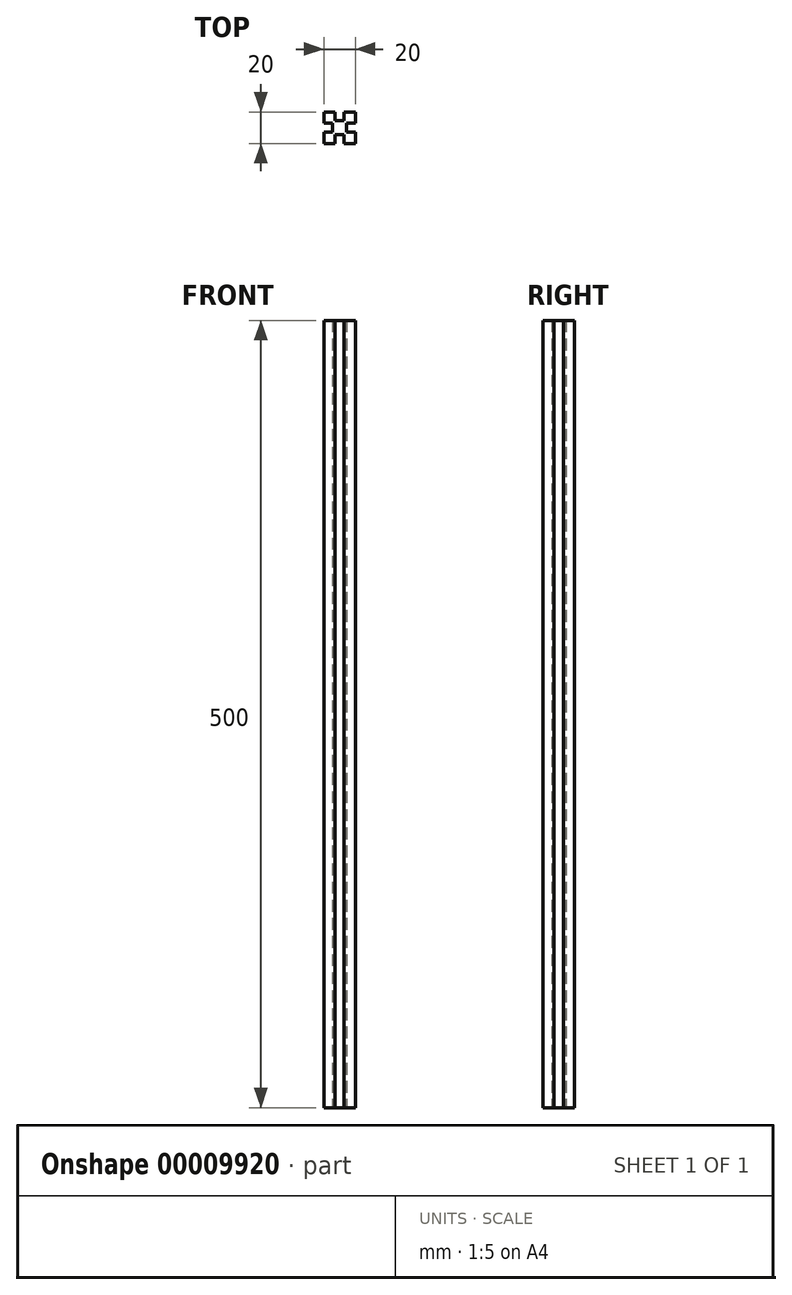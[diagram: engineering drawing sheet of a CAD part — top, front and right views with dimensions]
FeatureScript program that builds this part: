
annotation { "Feature Type Name" : "Feature", "Feature Type Description" : "" }
export const myFeature = defineFeature(function(context is Context, id is Id, definition is map)
    precondition{}
    {
        {
            var Q0;
            Q0=qCreatedBy(makeId("Top.planeOp"),FACE);
            var sketch = newSketch(context, id + "F0", { "sketchPlane" : qUnion([Q0])});
            skLineSegment(sketch, "E0.bottom", {"start": v(0, 0) * mm, "end": v(20, 0) * mm});
            skLineSegment(sketch, "E0.top", {"start": v(0, 20) * mm, "end": v(20, 20) * mm});
            skLineSegment(sketch, "E0.left", {"start": v(0, 0) * mm, "end": v(0, 20) * mm});
            skLineSegment(sketch, "E0.right", {"start": v(20, 0) * mm, "end": v(20, 20) * mm});
            skLineSegment(sketch, "E1.bottom", {"start": v(7, 20) * mm, "end": v(13, 20) * mm});
            skLineSegment(sketch, "E1.top", {"start": v(7, 14.5) * mm, "end": v(13, 14.5) * mm});
            skLineSegment(sketch, "E1.left", {"start": v(7, 20) * mm, "end": v(7, 14.5) * mm});
            skLineSegment(sketch, "E1.right", {"start": v(13, 20) * mm, "end": v(13, 14.5) * mm});
            skLineSegment(sketch, "E2.bottom", {"start": v(20, 13) * mm, "end": v(14.5, 13) * mm});
            skLineSegment(sketch, "E2.top", {"start": v(20, 7) * mm, "end": v(14.5, 7) * mm});
            skLineSegment(sketch, "E2.left", {"start": v(20, 13) * mm, "end": v(20, 7) * mm});
            skLineSegment(sketch, "E2.right", {"start": v(14.5, 13) * mm, "end": v(14.5, 7) * mm});
            skLineSegment(sketch, "E3.bottom", {"start": v(13, 0) * mm, "end": v(7, 0) * mm});
            skLineSegment(sketch, "E3.top", {"start": v(13, 5.5) * mm, "end": v(7, 5.5) * mm});
            skLineSegment(sketch, "E3.left", {"start": v(13, 0) * mm, "end": v(13, 5.5) * mm});
            skLineSegment(sketch, "E3.right", {"start": v(7, 0) * mm, "end": v(7, 5.5) * mm});
            skLineSegment(sketch, "E4.bottom", {"start": v(0, 7) * mm, "end": v(5.5, 7) * mm});
            skLineSegment(sketch, "E4.top", {"start": v(0, 13) * mm, "end": v(5.5, 13) * mm});
            skLineSegment(sketch, "E4.left", {"start": v(0, 7) * mm, "end": v(0, 13) * mm});
            skLineSegment(sketch, "E4.right", {"start": v(5.5, 7) * mm, "end": v(5.5, 13) * mm});
            skSolve(sketch);
        }
        {
            var Q0;
            Q0=makeQuery(id+"F0.imprint","IMPRINT",FACE,{"disambiguationData":[TD([[makeQuery(id+"F0.imprint","IMPRINT",EDGE,{"derivedFrom":sQuery(id+"F0.wireOp",EDGE,"E1.top")}),-1.0]])]});
            extrude(context, id + "F1", {"entities" : qUnion([Q0]), "depth" : 500 * mm});
        }
    });
